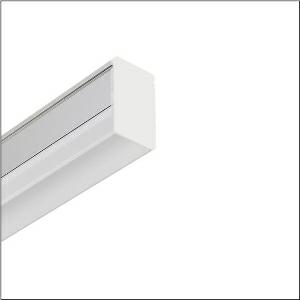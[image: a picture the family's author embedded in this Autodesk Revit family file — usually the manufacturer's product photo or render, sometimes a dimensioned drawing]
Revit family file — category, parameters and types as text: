
# Revit family: batten_41-f_51lp327km20af
name_source: partatom
category: Lighting Fixtures
units: mm (PartAtom-declared; Revit-internal decimal feet)

## family parameters
Cut with Voids When Loaded = No
Host = Face
Light Source = No
Part Type = Normal
Room Calculation Point = No
Round Connector Dimension = Use Diameter
Shared = No

## types (1)
- --- (1 x LED, 2000 lm, 16 W, 5000K)
    Apparent Load = 16 VA
    CIE Flux Codes = 37 66 87 87 100
    Color Rendering = 80
    Color Temperature = 5000K
    Default Elevation = 1800 mm
    Description = Batten 41-F, batten luminaire, primary optical cover: cover, of PC, frosted, light emission: direct distribution, primary light characteristic: symmetric, installation type: surface-mounted, LED, rated luminous flux: 2.000lm, luminous efficacy: 125lm/W, light colour: 830/840/850, colour temperature: 3000/4000/5000K, control gear: ON/OFF, with terminal, 2-pole, mains connection: 220..240V, AC, 50/60Hz, rated input power: 16W, housing, of aluminium, silver, length: 1.180mm, width: 25mm, height: 44mm, end cap, of PC, white, protection rating (complete): IP20, insulation class (complete): insulation class II (safety insulation), certification: CE, permissible operating ambient temperature: -20..+40°C, packaging unit: 1 piece
    Height = 44 mm
    Lamp = 1 x LED
    Lamp Light Flux = 2000 lm
    Lamp Power = 16 W
    Lamp count = 1
    Length = 1180 mm
    Luminous efficacy = 125 lm/W
    Manufacturer = Siteco
    ModVariant = No
    Model = 51LP327KM20AF
    Mounting Place = Ceiling
    Mounting Type = Surface mounted
    Number of Poles = 1
    OnlyDefault = Yes
    Power Factor = 1
    Product Name = Batten 41-F
    Product group = batten luminaire
    ProductGroupID = 303
    Protection Class = Protection class II
    Protection Degree = IP 20
    RLX_Detail_Level = 1
    RLX_Emergency_Light_Flux = 0 lm
    RLX_Emergency_Type = 0
    RLX_Emergency_Type_DB = No
    RlxData = <blob elided: 28273 chars, md5=472499c5>
    Socket = socket
    Standby Power = 0 W
    System Light Flux = 2000 lm
    System Power = 16 W
    Type Comments = individual setting: colour temperature 5000K
    Type Image = l_1007255.jpg
    URL = http://relux.com
    VarID = @adj_022790
    Voltage = 0 V
    Weight = 0.00 kg
    Width = 25 mm  [stored 0.082021 ft]

note: [stored X ft] marks values corroborated as IEEE doubles in the binary element streams (Revit-internal decimal feet)

## geometry (parser evidence)
native form markers: Blend x4, Sweep x12
no freeform markers — native parametric forms only
